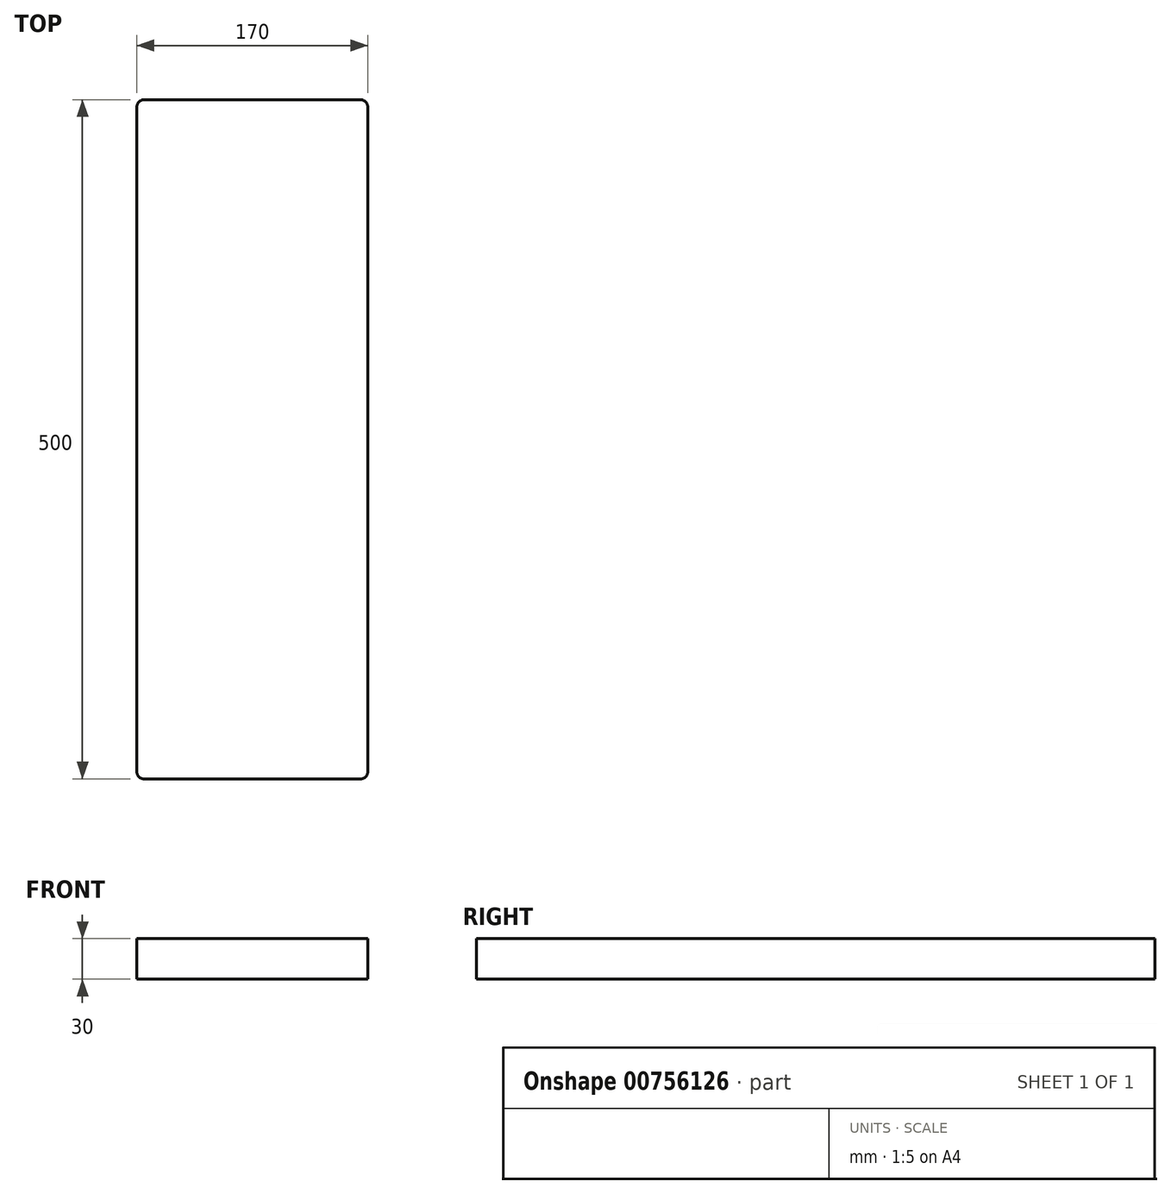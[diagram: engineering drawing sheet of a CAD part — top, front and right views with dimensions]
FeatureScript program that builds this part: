
annotation { "Feature Type Name" : "Feature", "Feature Type Description" : "" }
export const myFeature = defineFeature(function(context is Context, id is Id, definition is map)
    precondition{}
    {
        {
            var Q0;
            Q0=qCreatedBy(makeId("Front.planeOp"),FACE);
            var sketch = newSketch(context, id + "F0", { "sketchPlane" : qUnion([Q0])});
            skLineSegment(sketch, "E0.bottom", {"start": v(0, 0) * mm, "end": v(-170, 0) * mm});
            skLineSegment(sketch, "E0.top", {"start": v(0, -30) * mm, "end": v(-170, -30) * mm});
            skLineSegment(sketch, "E0.left", {"start": v(0, 0) * mm, "end": v(0, -30) * mm});
            skLineSegment(sketch, "E0.right", {"start": v(-170, 0) * mm, "end": v(-170, -30) * mm});
            skSolve(sketch);
        }
        {
            var Q0;
            Q0=makeQuery(id+"F0.imprint","IMPRINT",FACE,{"disambiguationData":[TD([[makeQuery(id+"F0.imprint","IMPRINT",EDGE,{"derivedFrom":sQuery(id+"F0.wireOp",EDGE,"E0.bottom")}),1.0]])]});
            extrude(context, id + "F1", {"entities" : qUnion([Q0]), "depth" : 500 * mm, "offsetDistance" : 25 * mm});
        }
        {
            var Q0;
            Q0=makeQuery(id+"F1.opExtrude","CAP_EDGE",EDGE,{"disambiguationData":[OSD([sQuery(id+"F0.wireOp",EDGE,"E0.left")])],"isStart":false});
            var Q1;
            Q1=makeQuery(id+"F1.opExtrude","CAP_EDGE",EDGE,{"disambiguationData":[OSD([sQuery(id+"F0.wireOp",EDGE,"E0.right")])],"isStart":false});
            var Q2;
            Q2=makeQuery(id+"F1.opExtrude","CAP_EDGE",EDGE,{"disambiguationData":[OSD([sQuery(id+"F0.wireOp",EDGE,"E0.right")])],"isStart":true});
            var Q3;
            Q3=makeQuery(id+"F1.opExtrude","CAP_EDGE",EDGE,{"disambiguationData":[OSD([sQuery(id+"F0.wireOp",EDGE,"E0.left")])],"isStart":true});
            fillet(context, id + "F2", {"entities" : qUnion([Q0, Q1, Q2, Q3]), "tangentPropagation" : true, "radius" : 5 * mm, "defaultsChanged" : false, "vertexSettings" : [], "allowEdgeOverflow" : false});
        }
    });
